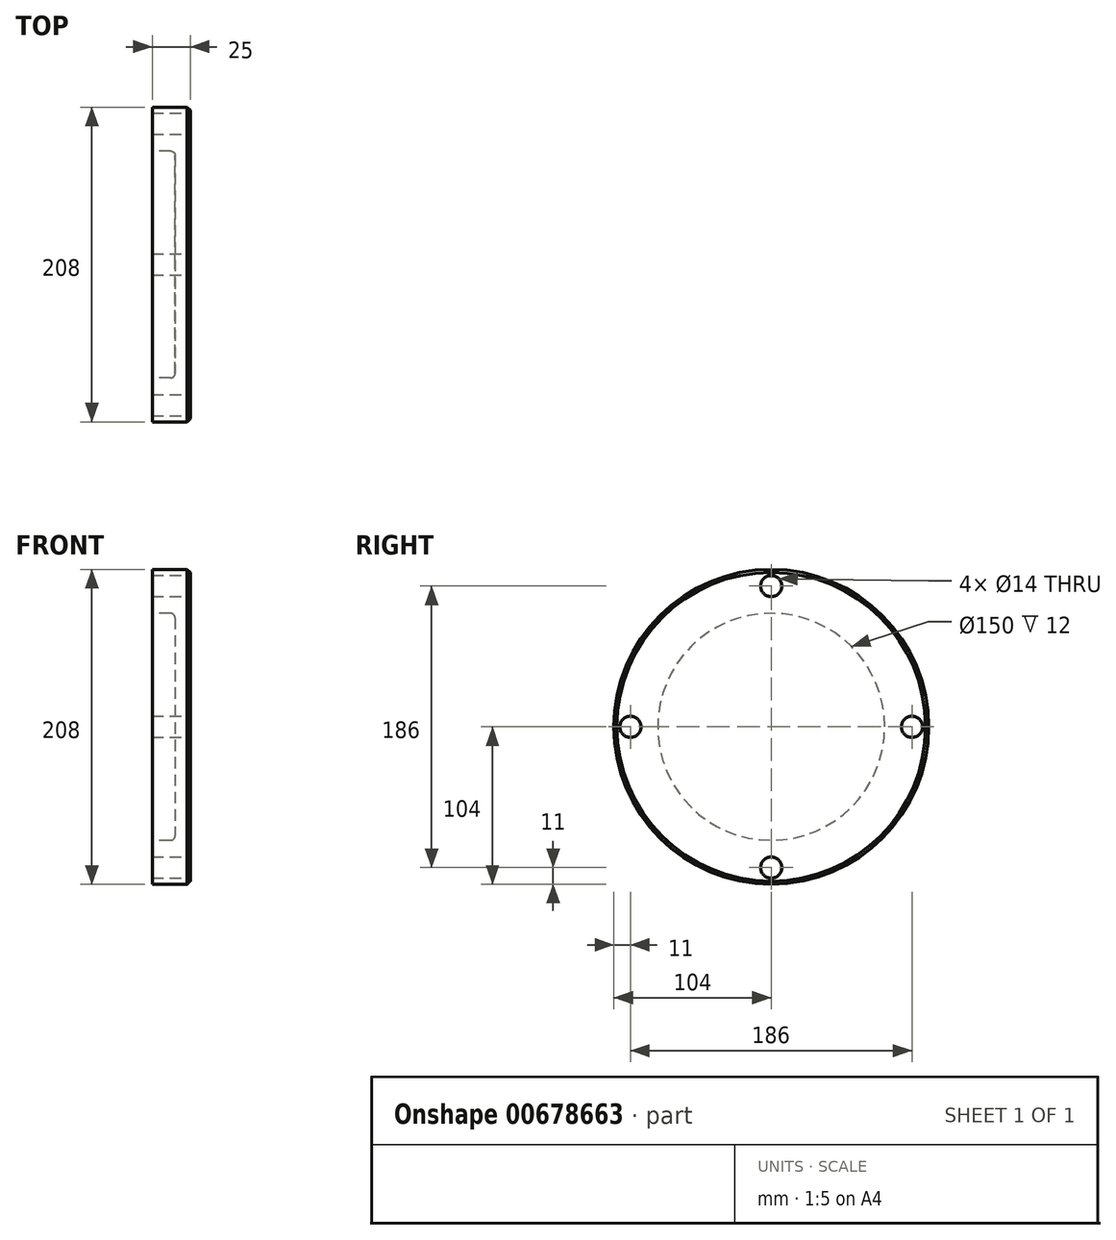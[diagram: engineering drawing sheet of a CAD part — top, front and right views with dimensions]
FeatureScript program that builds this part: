
annotation { "Feature Type Name" : "Feature", "Feature Type Description" : "" }
export const myFeature = defineFeature(function(context is Context, id is Id, definition is map)
    precondition{}
    {
        {
            var Q0;
            Q0=qCreatedBy(makeId("Right.planeOp"),FACE);
            var sketch = newSketch(context, id + "F0", { "sketchPlane" : qUnion([Q0])});
            skCircle(sketch, "E0", {"center": v(0, 0) * mm, "radius": 104 * mm});
            skSolve(sketch);
        }
        {
            var Q0;
            Q0 = qSketchRegion(id + "F0", true);
            extrude(context, id + "F1", {"entities" : qUnion([Q0]), "oppositeDirection" : true, "depth" : 25 * mm, "offsetDistance" : 25 * mm});
        }
        {
            var Q0;
            Q0=makeQuery(id+"F1.opExtrude","CAP_FACE",FACE,{"disambiguationData":[OSD([sQuery(id+"F0.wireOp",EDGE,"E0")])],"isStart":false});
            var sketch = newSketch(context, id + "F2", { "sketchPlane" : qUnion([Q0])});
            skCircle(sketch, "E1", {"center": v(0, 0) * mm, "radius": 75 * mm});
            skSolve(sketch);
        }
        {
            var Q0;
            Q0 = qSketchRegion(id + "F2", true);
            extrude(context, id + "F3", {"entities" : qUnion([Q0]), "operationType" : NewBodyOperationType.REMOVE, "oppositeDirection" : true, "depth" : 15 * mm, "offsetDistance" : 25 * mm});
        }
        {
            var Q0;
            Q0=makeQuery(id+"F3.boolean.opBoolean","COPY",EDGE,{"derivedFrom":makeQuery(id+"F3.opExtrude","CAP_EDGE",EDGE,{"disambiguationData":[OSD([sQuery(id+"F2.wireOp",EDGE,"E1")])],"isStart":false})});
            fillet(context, id + "F4", {"entities" : qUnion([Q0]), "radius" : 3 * mm, "tangentPropagation" : true, "allowEdgeOverflow" : false});
        }
        {
            var Q0;
            Q0=makeQuery(id+"F1.opExtrude","CAP_EDGE",EDGE,{"disambiguationData":[OSD([sQuery(id+"F0.wireOp",EDGE,"E0")])],"isStart":true});
            chamfer(context, id + "F5", {"entities" : qUnion([Q0]), "width" : 2 * mm, "tangentPropagation" : true});
        }
        {
            var Q0;
            Q0=makeQuery(id+"F1.opExtrude","CAP_FACE",FACE,{"disambiguationData":[OSD([sQuery(id+"F0.wireOp",EDGE,"E0")])],"isStart":true});
            var sketch = newSketch(context, id + "F6", { "sketchPlane" : qUnion([Q0])});
            skCircle(sketch, "E2", {"center": v(0, 0) * mm, "radius": 93 * mm, "construction": true});
            skLineSegment(sketch, "E3", {"start": v(0, 0) * mm, "end": v(0, 139.29) * mm, "construction": true});
            skPoint(sketch, "E4", {"position": v(0, 93) * mm});
            skPoint(sketch, "E5.1.0", {"position": v(-93, 0) * mm});
            skPoint(sketch, "E5.2.0", {"position": v(0, -93) * mm});
            skPoint(sketch, "E5.3.0", {"position": v(93, 0) * mm});
            skSolve(sketch);
        }
        {
            var Q0;
            Q0=sQuery(id+"F6.wireOp",VERTEX,"E4");
            var Q1;
            Q1=sQuery(id+"F6.wireOp",VERTEX,"E5.3.0");
            var Q2;
            Q2=sQuery(id+"F6.wireOp",VERTEX,"E5.2.0");
            var Q3;
            Q3=sQuery(id+"F6.wireOp",VERTEX,"E5.1.0");
            var Q4;
            Q4=makeQuery(id+"F1.opExtrude","SWEPT_BODY",BODY,{"disambiguationData":[OSD([sQuery(id+"F0.wireOp",EDGE,"E0")])]});
            hole(context, id + "F7", {"style" : HoleStyle.SIMPLE, "endStyle" : HoleEndStyle.THROUGH, "holeDiameter" : 14 * mm, "majorDiameter" : 5 * mm, "isTappedThrough" : true, "tappedDepth" : 24.75 * mm, "tapClearance" : 3, "locations" : qUnion([Q0, Q1, Q2, Q3]), "scope" : qUnion([Q4])});
        }
    });
